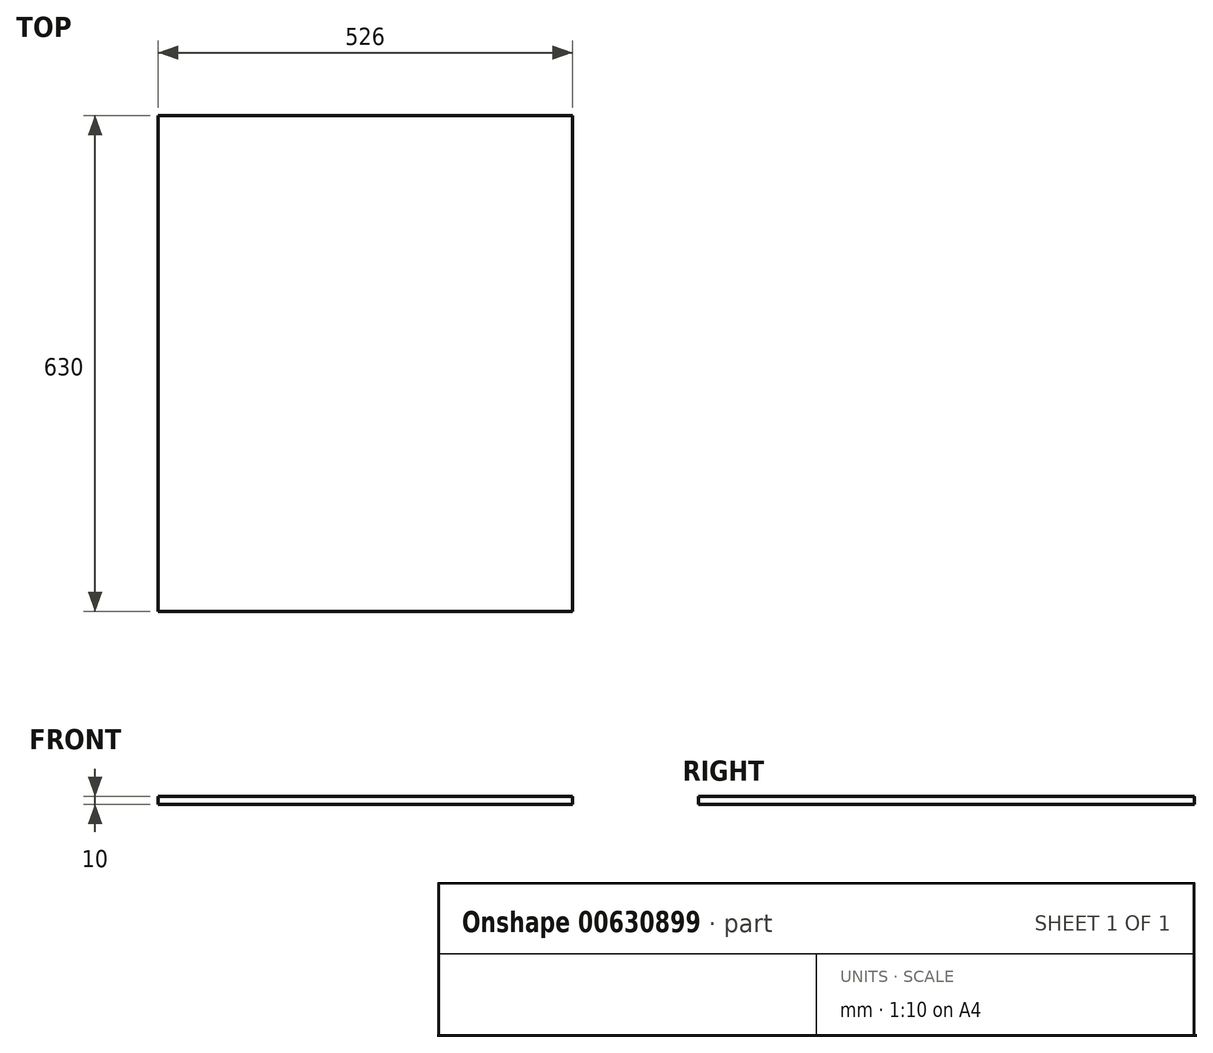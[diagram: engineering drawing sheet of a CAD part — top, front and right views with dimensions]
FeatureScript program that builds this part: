
annotation { "Feature Type Name" : "Feature", "Feature Type Description" : "" }
export const myFeature = defineFeature(function(context is Context, id is Id, definition is map)
    precondition{}
    {
        {
            var Q0;
            Q0=qCreatedBy(makeId("Top.planeOp"),FACE);
            var sketch = newSketch(context, id + "F0", { "sketchPlane" : qUnion([Q0])});
            skLineSegment(sketch, "E0.bottom", {"start": v(0, 630) * mm, "end": v(526, 630) * mm});
            skLineSegment(sketch, "E0.top", {"start": v(0, 0) * mm, "end": v(526, 0) * mm});
            skLineSegment(sketch, "E0.left", {"start": v(0, 630) * mm, "end": v(0, 0) * mm});
            skLineSegment(sketch, "E0.right", {"start": v(526, 630) * mm, "end": v(526, 0) * mm});
            skSolve(sketch);
        }
        {
            var Q0;
            Q0 = qSketchRegion(id + "F0", true);
            extrude(context, id + "F1", {"entities" : qUnion([Q0]), "depth" : 10 * mm, "offsetDistance" : 25 * mm});
        }
        {
            var Q0;
            Q0=makeQuery(id+"F1.opExtrude","SWEPT_FACE",FACE,{"disambiguationData":[OSD([sQuery(id+"F0.wireOp",EDGE,"E0.left")])]});
            var sketch = newSketch(context, id + "F2", { "sketchPlane" : qUnion([Q0])});
            skLineSegment(sketch, "E1", {"start": v(-630, 10) * mm, "end": v(-630, 460) * mm});
            skLineSegment(sketch, "E2", {"start": v(-630, 460) * mm, "end": v(-193.79, 460) * mm});
            skLineSegment(sketch, "E3", {"start": v(-193.79, 460) * mm, "end": v(-30, 10) * mm});
            skLineSegment(sketch, "E4", {"start": v(-30, 10) * mm, "end": v(-630, 10) * mm});
            skSolve(sketch);
        }
    });
